# Revit family: Lighting_Fixtures_Hill-Rom_TruLight1000
name_source: partatom
category: Lighting Fixtures
revit_build: Autodesk Revit Architecture 2015 (Build: 20140606_1530(x64)
units: mm (PartAtom-declared; Revit-internal decimal feet)

## types (1)
- TruLight 1000 Exam Light
    Apparent Load = 0 VA
    BIMobject category = Ceiling Mounted
    BIMobject category code = lighting-ceiling-mounted
    BIMobject main category = Lighting
    BIMobject main category code = lighting
    Brand url = https://construction.hill-rom.com
    Color Filter = 16777215
    Default Elevation = 4' - 0"
    Description = Wide range of applications
    Design country = United States
    Dimming Lamp Color Temperature Shift = <None>
    Edition number = 1
    Electrical Connector Description = Power supply
    Frequency Range = 50-60 Hz
    Illumination level Ec at 1m = 80000 lx
    Installation instructions = https://construction.hill-rom.com
    Light Source Symbol Size = 2' - 0"
    Manufacturer = Trumpf Medical
    Manufacturer country = United States
    Manufacturer name = Hill-Rom
    Masterformat 2014 Code = 26 55 70
    Masterformat 2014 Description = Healthcare Lighting
    Material_red = Plastic-Hill-Rom-Transparent Red
    Material_white = Plastic-Hill-Rom-White
    Max Amperage = 0 A
    Model = Tru Light 1000 Exam Light
    Nominal height = 0' - 0"
    Nominal width = 0' - 0"
    OmniClass Code = 23-35 47 11 21
    OmniClass Description = Specialized Lighting Fixtures
    Power Factor = 1
    Product Guid = 3232bf26-4a15-4f58-a262-8c42eeaabcd1
    Product SKU = Trumpf-TruLight1000
    Product certification = https://www.trumpfmedical.com
    Product data url = https://bimobject.com
    Product family = Exam Lights
    Product group = TruLight1000
    Product url = https://www.trumpfmedical.com
    QR code = http://bimobject.com
    Technical description = https://construction.hill-rom.com
    UNSPSC Code = 39101602
    URL = www.hill-rom.com/

/www.hill-rom.com/

/www.hill-rom.com/

www.hill-rom.com
    Uniclass 1.4 Code = L747331
    Uniclass 1.4 Description = Medical/hospital lighting
    Voltage = 120 V
    Voltage Range = 100-240 V
    Weight Net (Kg) = 0
    Youtube clip = https://www.youtube.com

## geometry (parser evidence)
native form markers: Blend x4, Sweep x2
no freeform markers — native parametric forms only
